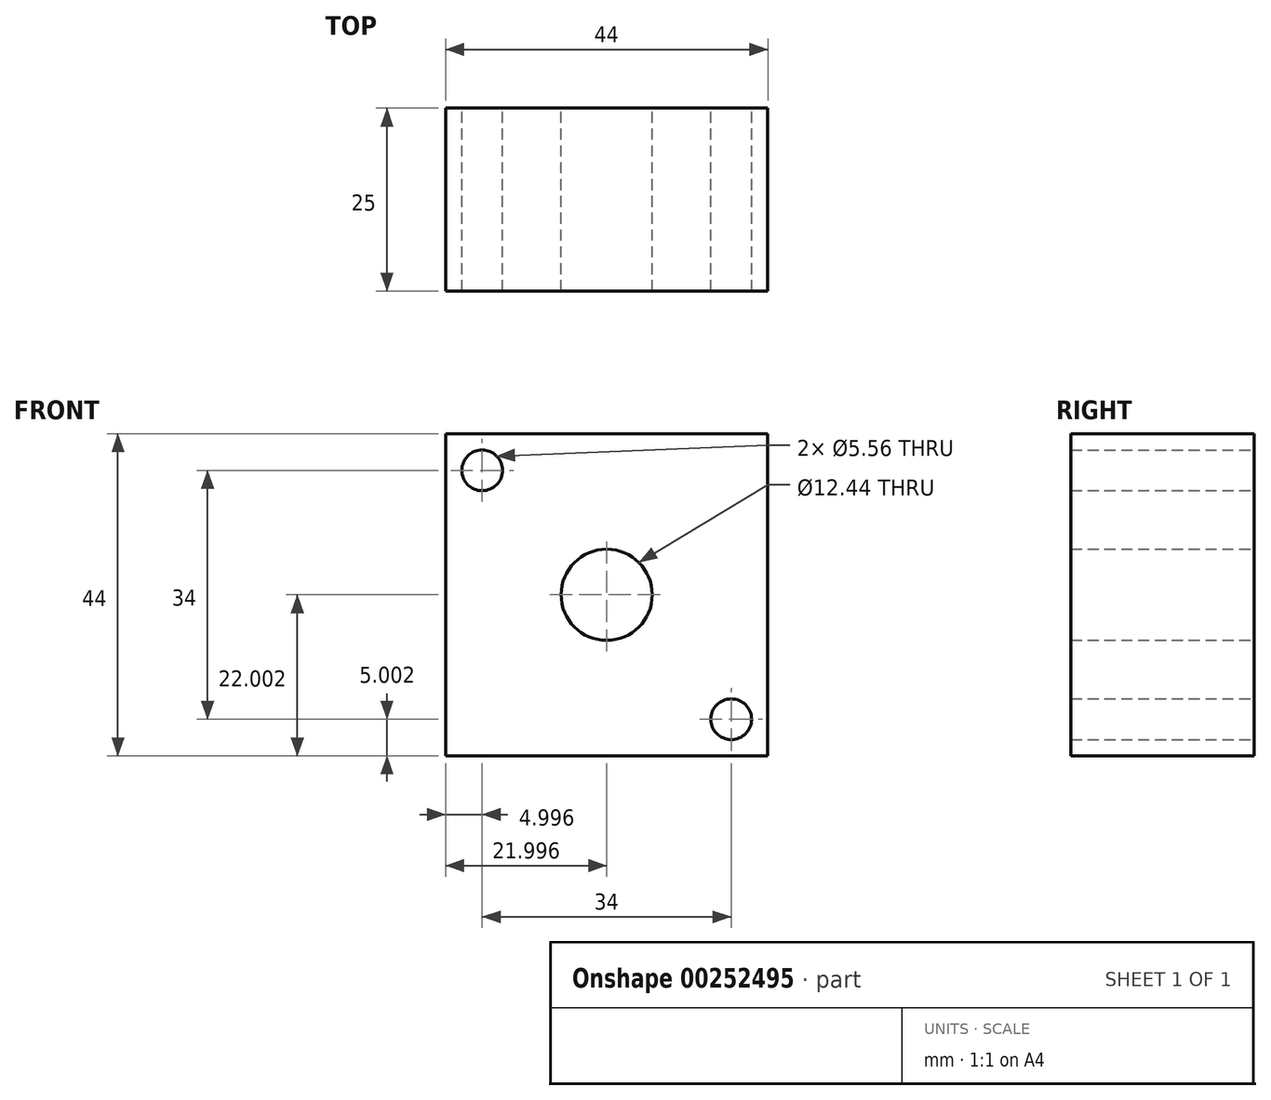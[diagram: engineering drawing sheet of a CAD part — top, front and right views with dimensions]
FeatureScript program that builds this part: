
annotation { "Feature Type Name" : "Feature", "Feature Type Description" : "" }
export const myFeature = defineFeature(function(context is Context, id is Id, definition is map)
    precondition{}
    {
        {
            var Q0;
            Q0=qCreatedBy(makeId("Front.planeOp"),FACE);
            var sketch = newSketch(context, id + "F0", { "sketchPlane" : qUnion([Q0])});
            skLineSegment(sketch, "E0.bottom", {"start": v(36.22, 24.03) * mm, "end": v(80.22, 24.03) * mm});
            skLineSegment(sketch, "E0.top", {"start": v(36.22, 68.03) * mm, "end": v(80.22, 68.03) * mm});
            skLineSegment(sketch, "E0.left", {"start": v(36.22, 24.03) * mm, "end": v(36.22, 68.03) * mm});
            skLineSegment(sketch, "E0.right", {"start": v(80.22, 24.03) * mm, "end": v(80.22, 68.03) * mm});
            skLineSegment(sketch, "E1", {"start": v(80.22, 68.03) * mm, "end": v(80.22, 89.88) * mm, "construction": true});
            skLineSegment(sketch, "E2", {"start": v(80.22, 68.03) * mm, "end": v(87.17, 74.99) * mm, "construction": true});
            skCircle(sketch, "E3", {"center": v(41.22, 63.03) * mm, "radius": 2.78 * mm});
            skCircle(sketch, "E4.MirrorC", {"center": v(75.22, 29.03) * mm, "radius": 2.78 * mm});
            skCircle(sketch, "E5", {"center": v(58.22, 46.03) * mm, "radius": 6.22 * mm});
            skPoint(sketch, "E5.centerSnap0", {"position": v(36.22, 46.03) * mm});
            skPoint(sketch, "E5.centerSnap1", {"position": v(58.22, 68.03) * mm});
            skSolve(sketch);
        }
        {
            var Q0;
            Q0=makeQuery(id+"F0.imprint","IMPRINT",FACE,{"disambiguationData":[TD([[makeQuery(id+"F0.imprint","IMPRINT",EDGE,{"derivedFrom":sQuery(id+"F0.wireOp",EDGE,"E0.bottom")}),1.0]])]});
            extrude(context, id + "F1", {"entities" : qUnion([Q0]), "depth" : 25 * mm});
        }
    });
